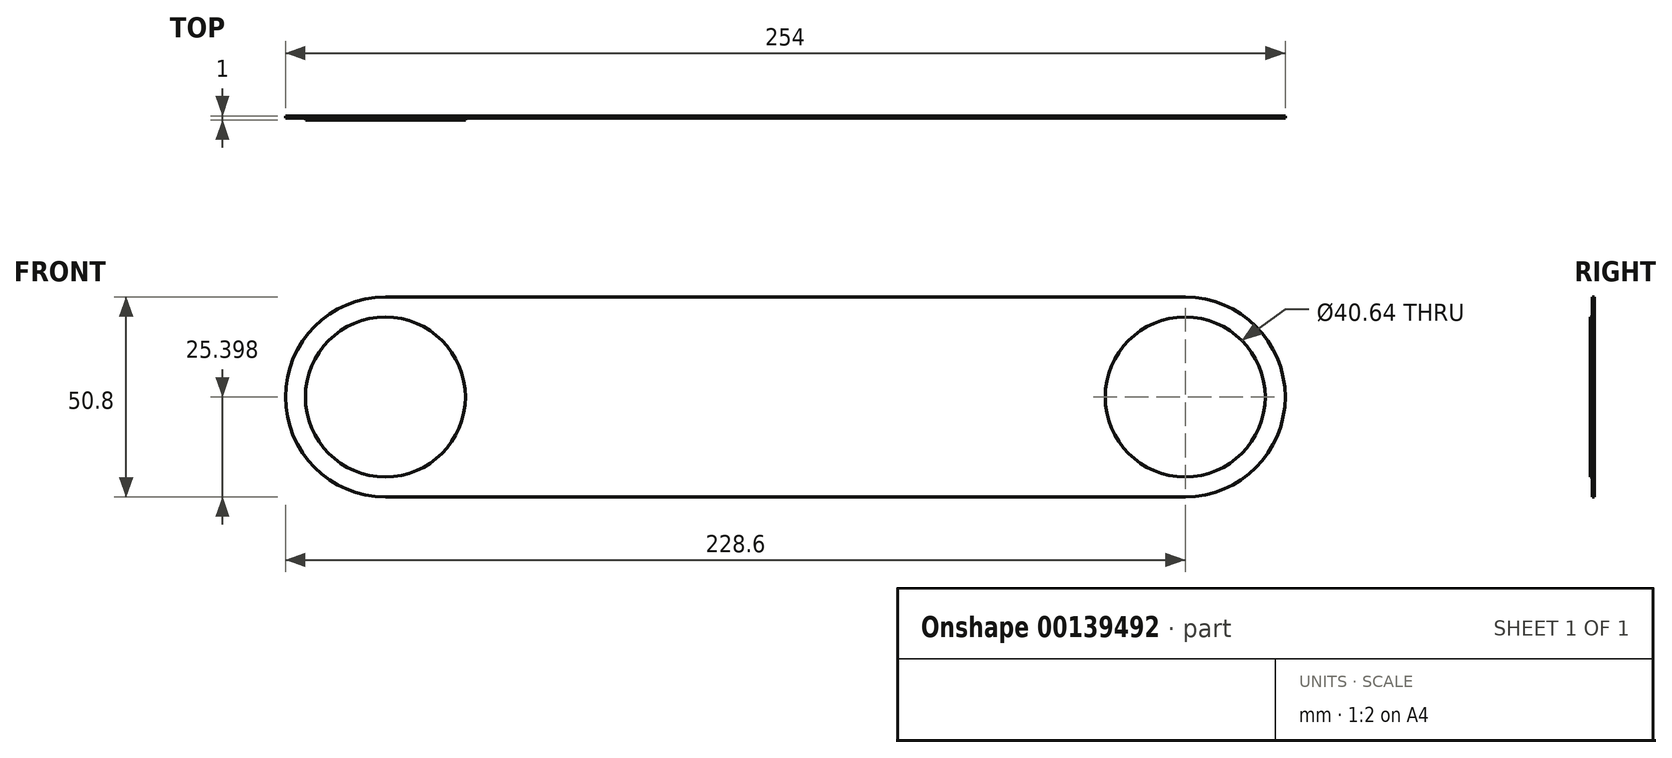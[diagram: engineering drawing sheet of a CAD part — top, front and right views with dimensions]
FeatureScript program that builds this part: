
annotation { "Feature Type Name" : "Feature", "Feature Type Description" : "" }
export const myFeature = defineFeature(function(context is Context, id is Id, definition is map)
    precondition{}
    {
        {
            assignVariable(context, id + "F0", {"name" : "D", "anyValue" : .5});
        }
        {
            var Q0;
            Q0=qCreatedBy(makeId("Front.planeOp"),FACE);
            var sketch = newSketch(context, id + "F1", { "sketchPlane" : qUnion([Q0])});
            skLineSegment(sketch, "E0.bottom", {"start": v(-50.85, 52.24) * mm, "end": v(152.35, 52.24) * mm});
            skLineSegment(sketch, "E0.top", {"start": v(-50.85, 1.44) * mm, "end": v(152.35, 1.44) * mm});
            skLineSegment(sketch, "E0.left", {"start": v(-76.25, 26.84) * mm, "end": v(-76.25, 26.84) * mm});
            skLineSegment(sketch, "E0.right", {"start": v(177.75, 26.84) * mm, "end": v(177.75, 26.84) * mm});
            skPoint(sketch, "E1.visualSharp", {"position": v(-76.25, 52.24) * mm});
            skArc(sketch, "E1.filletArc", {"start": v(-50.85, 52.24) * mm, "mid": v(-68.81, 44.8) * mm, "end": v(-76.25, 26.84) * mm});
            skPoint(sketch, "E2.visualSharp", {"position": v(-76.25, 1.44) * mm});
            skArc(sketch, "E2.filletArc", {"start": v(-76.25, 26.84) * mm, "mid": v(-68.81, 8.88) * mm, "end": v(-50.85, 1.44) * mm});
            skPoint(sketch, "E3.visualSharp", {"position": v(177.75, 1.44) * mm});
            skArc(sketch, "E3.filletArc", {"start": v(152.35, 1.44) * mm, "mid": v(170.31, 8.88) * mm, "end": v(177.75, 26.84) * mm});
            skPoint(sketch, "E4.visualSharp", {"position": v(177.75, 52.24) * mm});
            skArc(sketch, "E4.filletArc", {"start": v(177.75, 26.84) * mm, "mid": v(170.31, 44.8) * mm, "end": v(152.35, 52.24) * mm});
            skSolve(sketch);
        }
        {
            var Q0;
            Q0=makeQuery(id+"F1.imprint","IMPRINT",FACE,{"disambiguationData":[TD([[makeQuery(id+"F1.imprint","IMPRINT",EDGE,{"derivedFrom":sQuery(id+"F1.wireOp",EDGE,"E0.bottom")}),-1.0]])]});
            extrude(context, id + "F2", {"entities" : qUnion([Q0]), "depth" : (getVariable(context, 'D')) * mm});
        }
        {
            var Q0;
            Q0=makeQuery(id+"F2.opExtrude","CAP_FACE",FACE,{"disambiguationData":[OSD([sQuery(id+"F1.wireOp",EDGE,"E0.bottom"),sQuery(id+"F1.wireOp",EDGE,"E0.top"),sQuery(id+"F1.wireOp",EDGE,"E1.filletArc"),sQuery(id+"F1.wireOp",EDGE,"E2.filletArc"),sQuery(id+"F1.wireOp",EDGE,"E3.filletArc"),sQuery(id+"F1.wireOp",EDGE,"E4.filletArc")])],"isStart":false});
            var sketch = newSketch(context, id + "F3", { "sketchPlane" : qUnion([Q0])});
            skCircle(sketch, "E5", {"center": v(-50.85, 26.84) * mm, "radius": 20.32 * mm});
            skCircle(sketch, "E6", {"center": v(152.35, 26.84) * mm, "radius": 20.32 * mm});
            skSolve(sketch);
        }
        {
            var Q0;
            Q0=makeQuery(id+"F3.imprint","IMPRINT",FACE,{"disambiguationData":[TD([[makeQuery(id+"F3.imprint","IMPRINT",EDGE,{"derivedFrom":sQuery(id+"F3.wireOp",EDGE,"E5")}),1.0]])]});
            extrude(context, id + "F4", {"entities" : qUnion([Q0]), "operationType" : NewBodyOperationType.ADD, "depth" : (getVariable(context, 'D')) * mm});
        }
        {
            var Q0;
            Q0=makeQuery(id+"F3.imprint","IMPRINT",FACE,{"disambiguationData":[TD([[makeQuery(id+"F3.imprint","IMPRINT",EDGE,{"derivedFrom":sQuery(id+"F3.wireOp",EDGE,"E6")}),1.0]])]});
            extrude(context, id + "F5", {"entities" : qUnion([Q0]), "operationType" : NewBodyOperationType.REMOVE, "oppositeDirection" : true, "depth" : (getVariable(context, 'D')) * mm});
        }
    });
